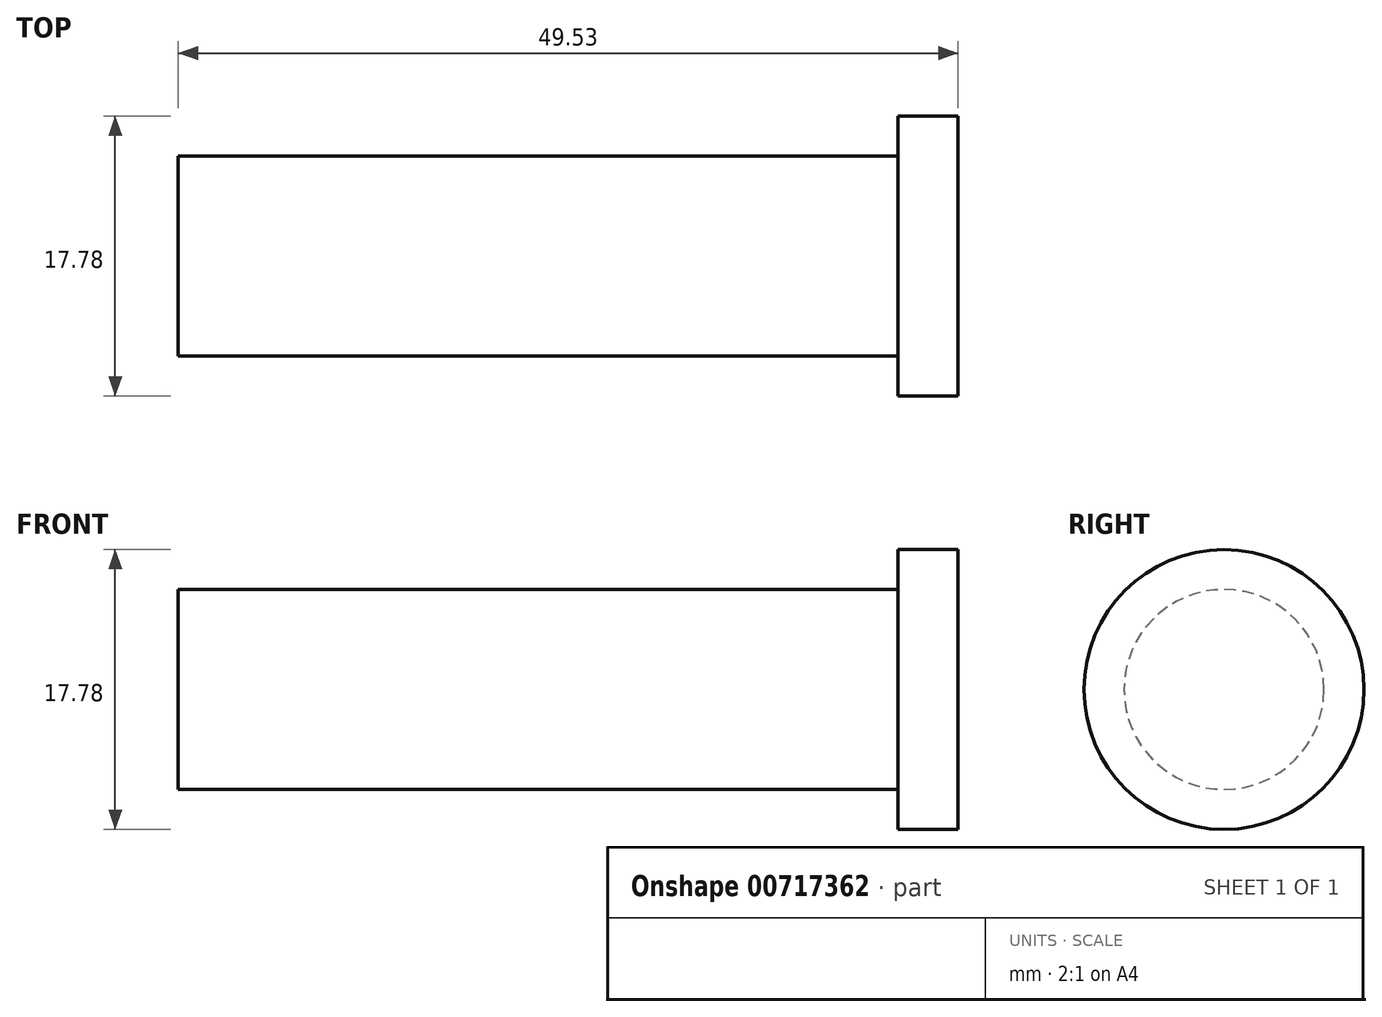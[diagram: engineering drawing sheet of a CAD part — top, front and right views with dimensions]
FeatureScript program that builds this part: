
annotation { "Feature Type Name" : "Feature", "Feature Type Description" : "" }
export const myFeature = defineFeature(function(context is Context, id is Id, definition is map)
    precondition{}
    {
        {
            var Q0;
            Q0=qCreatedBy(makeId("Right.planeOp"),FACE);
            var sketch = newSketch(context, id + "F0", { "sketchPlane" : qUnion([Q0])});
            skCircle(sketch, "E0", {"center": v(0, 0) * mm, "radius": 6.35 * mm});
            skSolve(sketch);
        }
        {
            var Q0;
            Q0=makeQuery(id+"F0.imprint","IMPRINT",FACE,{"disambiguationData":[TD([[makeQuery(id+"F0.imprint","IMPRINT",EDGE,{"derivedFrom":sQuery(id+"F0.wireOp",EDGE,"E0")}),1.0]])]});
            extrude(context, id + "F1", {"entities" : qUnion([Q0]), "depth" : 45.72 * mm, "offsetDistance" : 25.4 * mm});
        }
        {
            var Q0;
            Q0=makeQuery(id+"F1.opExtrude","CAP_FACE",FACE,{"disambiguationData":[OSD([sQuery(id+"F0.wireOp",EDGE,"E0")])],"isStart":false});
            var sketch = newSketch(context, id + "F2", { "sketchPlane" : qUnion([Q0])});
            skCircle(sketch, "E1", {"center": v(0, 0) * mm, "radius": 8.9 * mm});
            skSolve(sketch);
        }
        {
            var Q0;
            Q0=makeQuery(id+"F2.imprint","IMPRINT",FACE,{"disambiguationData":[TD([[makeQuery(id+"F2.imprint","IMPRINT",EDGE,{"derivedFrom":sQuery(id+"F2.wireOp",EDGE,"E1")}),1.0]])]});
            var Q1;
            Q1=makeQuery(id+"F2.imprint","IMPRINT",FACE,{"disambiguationData":[TD([[makeQuery(id+"F2.imprint","IMPRINT",EDGE,{"derivedFrom":makeQuery(id+"F1.opExtrude","CAP_EDGE",EDGE,{"disambiguationData":[OSD([sQuery(id+"F0.wireOp",EDGE,"E0")])],"isStart":false})}),1.0]])]});
            extrude(context, id + "F3", {"entities" : qUnion([Q0, Q1]), "operationType" : NewBodyOperationType.ADD, "depth" : 3.8 * mm, "offsetDistance" : 25.4 * mm});
        }
    });
